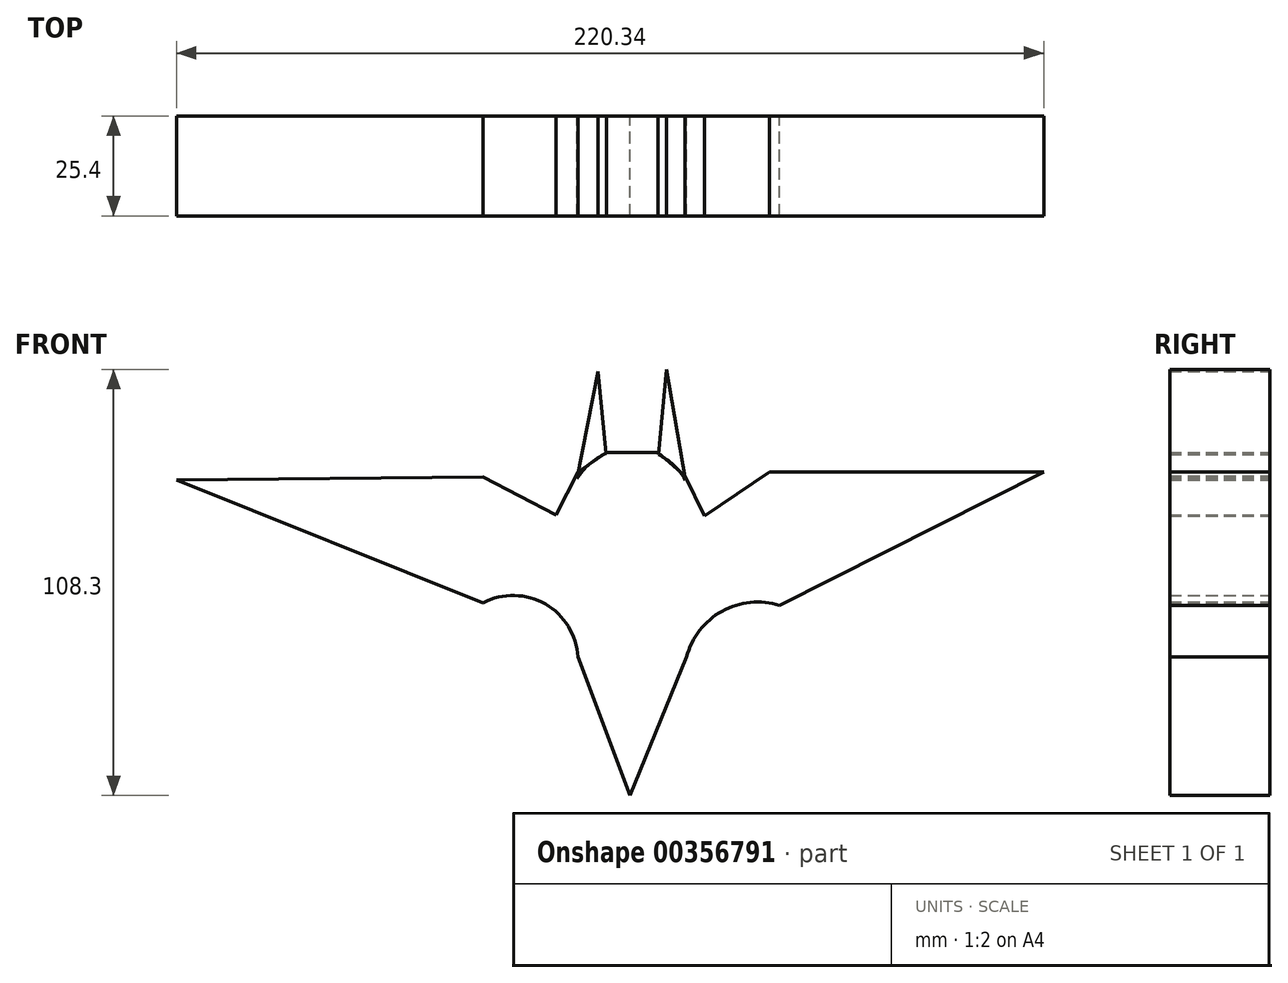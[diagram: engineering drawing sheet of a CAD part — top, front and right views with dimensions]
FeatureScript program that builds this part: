
annotation { "Feature Type Name" : "Feature", "Feature Type Description" : "" }
export const myFeature = defineFeature(function(context is Context, id is Id, definition is map)
    precondition{}
    {
        {
            var Q0;
            Q0=qCreatedBy(makeId("Front.planeOp"),FACE);
            var sketch = newSketch(context, id + "F0", { "sketchPlane" : qUnion([Q0])});
            skArc(sketch, "E0", {"start": v(14.04, 45.02) * mm, "mid": v(0.4, 53) * mm, "end": v(-13.42, 45.32) * mm});
            skLineSegment(sketch, "E1", {"start": v(7.18, 51.4) * mm, "end": v(9.31, 73.07) * mm});
            skLineSegment(sketch, "E2", {"start": v(9.31, 73.07) * mm, "end": v(14.04, 45.02) * mm});
            skLineSegment(sketch, "E3", {"start": v(-13.42, 45.32) * mm, "end": v(-8.1, 72.48) * mm});
            skLineSegment(sketch, "E4", {"start": v(-8.1, 72.48) * mm, "end": v(-6.1, 51.69) * mm});
            skArc(sketch, "E5", {"start": v(-37.04, 45.32) * mm, "mid": v(-25.23, 35.6) * mm, "end": v(-13.42, 45.32) * mm});
            skArc(sketch, "E6", {"start": v(14.04, 45.02) * mm, "mid": v(25.7, 35.16) * mm, "end": v(37.36, 45.02) * mm});
            skLineSegment(sketch, "E7", {"start": v(37.36, 45.02) * mm, "end": v(123.86, 45.02) * mm});
            skLineSegment(sketch, "E8", {"start": v(123.86, 45.02) * mm, "end": v(37.36, 12.46) * mm});
            skSolve(sketch);
        }
        {
            var Q0;
            {var subQ2=sQuery(id+"F0.wireOp",EDGE,"E1");Q0=makeQuery(id+"F0.imprint","IMPRINT",FACE,{"disambiguationData":[TD([[makeQuery(id+"F0.imprint","IMPRINT",EDGE,{"derivedFrom":subQ2}),-1.0]])]});}
            var Q1;
            {var subQ0=sQuery(id+"F0.wireOp",EDGE,"E3");Q1=makeQuery(id+"F0.imprint","IMPRINT",FACE,{"disambiguationData":[TD([[makeQuery(id+"F0.imprint","IMPRINT",EDGE,{"derivedFrom":subQ0}),-1.0]])]});}
            extrude(context, id + "F1", {"entities" : qUnion([Q0, Q1]), "depth" : 25.4 * mm, "offsetDistance" : 25.4 * mm});
        }
        {
            var Q0;
            Q0=qCreatedBy(makeId("Front.planeOp"),FACE);
            var sketch = newSketch(context, id + "F2", { "sketchPlane" : qUnion([Q0])});
            skLineSegment(sketch, "E9", {"start": v(-37.28, 45.67) * mm, "end": v(-18.86, 36.14) * mm});
            skLineSegment(sketch, "E10", {"start": v(-18.86, 36.14) * mm, "end": v(-13.24, 47) * mm});
            skLineSegment(sketch, "E11", {"start": v(-13.24, 47) * mm, "end": v(-6.04, 51.92) * mm});
            skLineSegment(sketch, "E12", {"start": v(-6.04, 51.92) * mm, "end": v(7.12, 51.92) * mm});
            skLineSegment(sketch, "E13", {"start": v(7.12, 51.92) * mm, "end": v(14.02, 46) * mm});
            skLineSegment(sketch, "E14", {"start": v(14.02, 46) * mm, "end": v(18.96, 35.8) * mm});
            skLineSegment(sketch, "E15", {"start": v(18.96, 35.8) * mm, "end": v(35.4, 46.99) * mm});
            skLineSegment(sketch, "E16", {"start": v(35.4, 46.99) * mm, "end": v(105.12, 46.99) * mm});
            skLineSegment(sketch, "E17", {"start": v(105.12, 46.99) * mm, "end": v(38.03, 13.12) * mm});
            skArc(sketch, "E18", {"start": v(38.03, 13.12) * mm, "mid": v(23.39, 11.62) * mm, "end": v(14.35, 0) * mm});
            skLineSegment(sketch, "E19", {"start": v(14.35, 0) * mm, "end": v(0, -35.23) * mm});
            skLineSegment(sketch, "E20", {"start": v(0, -35.23) * mm, "end": v(-13.27, 0) * mm});
            skArc(sketch, "E21", {"start": v(-13.27, 0) * mm, "mid": v(-21.52, 13.43) * mm, "end": v(-37.28, 13.77) * mm});
            skLineSegment(sketch, "E22", {"start": v(-37.28, 13.77) * mm, "end": v(-115.22, 45.01) * mm});
            skLineSegment(sketch, "E23", {"start": v(-115.22, 45.01) * mm, "end": v(-37.28, 45.67) * mm});
            skSolve(sketch);
        }
        {
            var Q0;
            Q0=makeQuery(id+"F2.imprint","IMPRINT",FACE,{"disambiguationData":[TD([[makeQuery(id+"F2.imprint","IMPRINT",EDGE,{"derivedFrom":sQuery(id+"F2.wireOp",EDGE,"E9")}),-1.0]])]});
            extrude(context, id + "F3", {"entities" : qUnion([Q0]), "depth" : 25.4 * mm, "offsetDistance" : 25.4 * mm});
        }
    });
